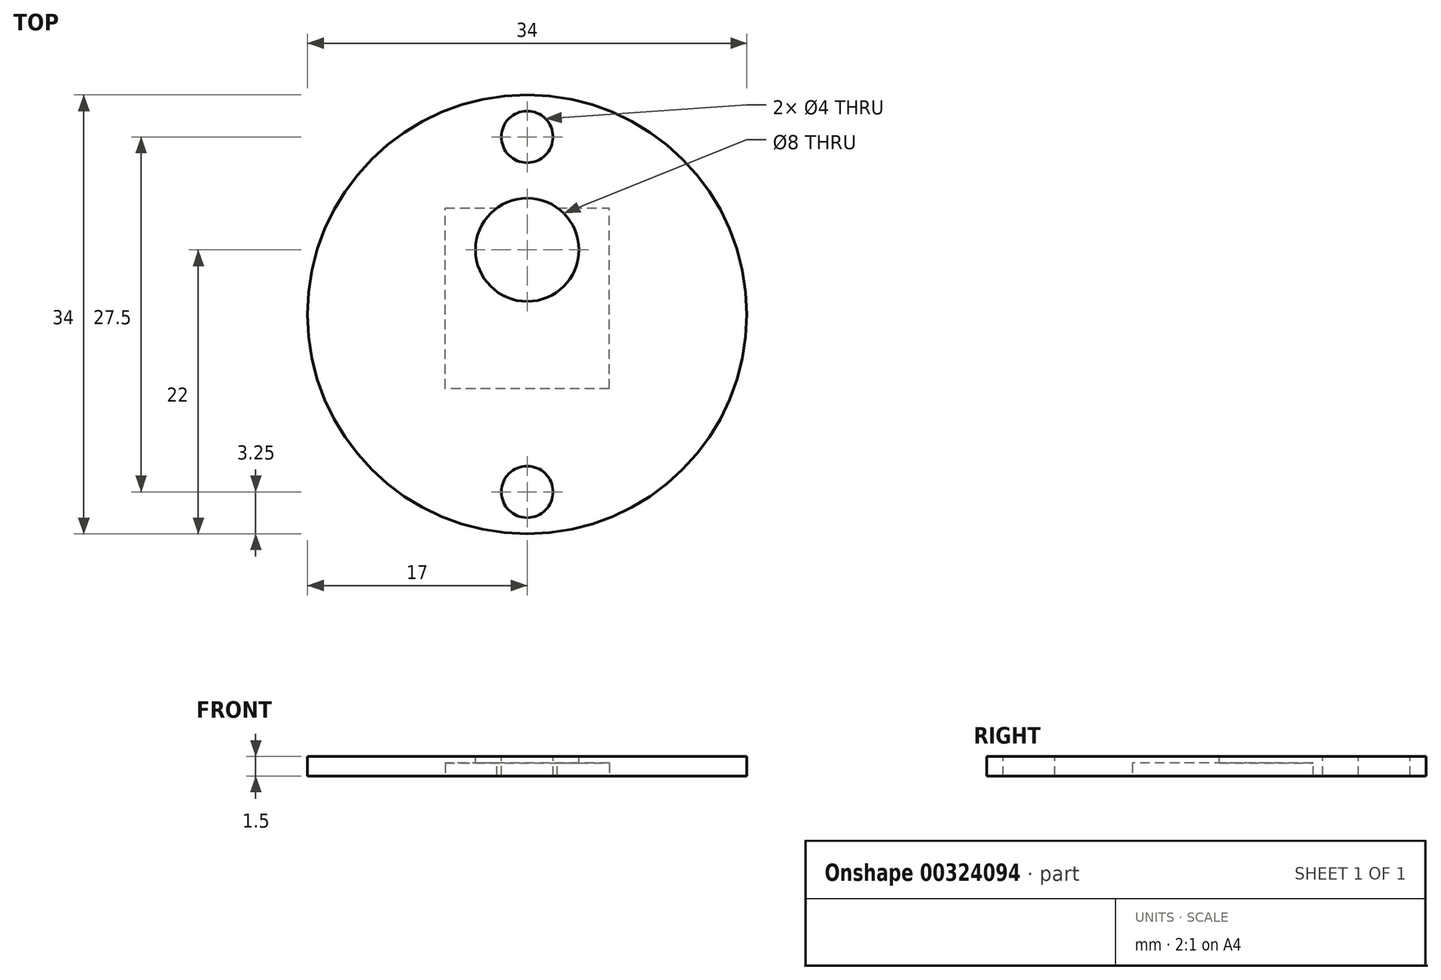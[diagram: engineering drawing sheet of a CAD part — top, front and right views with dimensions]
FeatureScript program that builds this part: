
annotation { "Feature Type Name" : "Feature", "Feature Type Description" : "" }
export const myFeature = defineFeature(function(context is Context, id is Id, definition is map)
    precondition{}
    {
        {
            var Q0;
            Q0=qCreatedBy(makeId("Top.planeOp"),FACE);
            var sketch = newSketch(context, id + "F0", { "sketchPlane" : qUnion([Q0])});
            skCircle(sketch, "E0", {"center": v(0, 0) * mm, "radius": 9.1 * mm});
            skLineSegment(sketch, "E1.bottom", {"start": v(-6.35, 5.75) * mm, "end": v(6.35, 5.75) * mm});
            skLineSegment(sketch, "E1.top", {"start": v(-6.35, -5.75) * mm, "end": v(6.35, -5.75) * mm});
            skLineSegment(sketch, "E1.left", {"start": v(-6.35, 5.75) * mm, "end": v(-6.35, -5.75) * mm});
            skLineSegment(sketch, "E1.right", {"start": v(6.35, 5.75) * mm, "end": v(6.35, -5.75) * mm});
            skSolve(sketch);
        }
        {
            var Q0;
            Q0=makeQuery(id+"F0.imprint","IMPRINT",FACE,{"disambiguationData":[TD([[makeQuery(id+"F0.imprint","IMPRINT",EDGE,{"derivedFrom":sQuery(id+"F0.wireOp",EDGE,"E0")}),1.0]])]});
            extrude(context, id + "F1", {"entities" : qUnion([Q0]), "depth" : 14 * mm});
        }
        {
            var Q0;
            Q0=makeQuery(id+"F1.opExtrude","CAP_FACE",FACE,{"disambiguationData":[OSD([sQuery(id+"F0.wireOp",EDGE,"E0"),sQuery(id+"F0.wireOp",EDGE,"E1.bottom"),sQuery(id+"F0.wireOp",EDGE,"E1.top"),sQuery(id+"F0.wireOp",EDGE,"E1.left"),sQuery(id+"F0.wireOp",EDGE,"E1.right")])],"isStart":true});
            var sketch = newSketch(context, id + "F2", { "sketchPlane" : qUnion([Q0])});
            skLineSegment(sketch, "E2.bottom", {"start": v(6.35, -3.25) * mm, "end": v(-6.35, -3.25) * mm});
            skLineSegment(sketch, "E2.top", {"start": v(6.35, -8.25) * mm, "end": v(-6.35, -8.25) * mm});
            skLineSegment(sketch, "E2.left", {"start": v(6.35, -3.25) * mm, "end": v(6.35, -8.25) * mm});
            skLineSegment(sketch, "E2.right", {"start": v(-6.35, -3.25) * mm, "end": v(-6.35, -8.25) * mm});
            skPoint(sketch, "E2.middle", {"position": v(0, -5.75) * mm});
            skSolve(sketch);
        }
        {
            var Q0;
            {var subQ1=makeQuery(id+"F1.opExtrude","CAP_EDGE",EDGE,{"disambiguationData":[OSD([sQuery(id+"F0.wireOp",EDGE,"E1.bottom")])],"isStart":true});Q0=makeQuery(id+"F2.imprint","IMPRINT",FACE,{"disambiguationData":[TD([[makeQuery(id+"F2.imprint","IMPRINT",EDGE,{"derivedFrom":subQ1}),-1.0]])]});}
            extrude(context, id + "F3", {"entities" : qUnion([Q0]), "operationType" : NewBodyOperationType.REMOVE, "oppositeDirection" : true, "depth" : 5 * mm});
        }
        {
            var Q0;
            Q0=makeQuery(id+"F1.opExtrude","CAP_FACE",FACE,{"disambiguationData":[OSD([sQuery(id+"F0.wireOp",EDGE,"E0"),sQuery(id+"F0.wireOp",EDGE,"E1.bottom"),sQuery(id+"F0.wireOp",EDGE,"E1.top"),sQuery(id+"F0.wireOp",EDGE,"E1.left"),sQuery(id+"F0.wireOp",EDGE,"E1.right")])],"isStart":false});
            cPlane(context, id + "F4", {"entities" : qUnion([Q0]), "cplaneType" : CPlaneType.OFFSET, "offset" : 10 * mm, "oppositeDirection" : true, "width" : 150 * mm, "height" : 150 * mm});
        }
        {
            var Q0;
            Q0=qCreatedBy(id+"F4.planeOp",FACE);
            var sketch = newSketch(context, id + "F5", { "sketchPlane" : qUnion([Q0])});
            skCircle(sketch, "E3", {"center": v(0, 0) * mm, "radius": 17 * mm});
            skCircle(sketch, "E4", {"center": v(0, 0) * mm, "radius": 13.75 * mm, "construction": true});
            skCircle(sketch, "E5", {"center": v(0, 5) * mm, "radius": 4 * mm});
            skCircle(sketch, "E6", {"center": v(0, 13.75) * mm, "radius": 2 * mm});
            skCircle(sketch, "E7", {"center": v(0, -13.75) * mm, "radius": 2 * mm});
            skSolve(sketch);
        }
        {
            var Q0;
            Q0=qSketchRegion(id+"F5",true);
            extrude(context, id + "F6", {"entities" : qUnion([Q0]), "oppositeDirection" : true, "depth" : 1.5 * mm});
        }
        {
            var Q0;
            Q0=makeQuery(id+"F1.opExtrude","SWEPT_BODY",BODY,{"disambiguationData":[OSD([sQuery(id+"F0.wireOp",EDGE,"E0"),sQuery(id+"F0.wireOp",EDGE,"E1.bottom"),sQuery(id+"F0.wireOp",EDGE,"E1.top"),sQuery(id+"F0.wireOp",EDGE,"E1.left"),sQuery(id+"F0.wireOp",EDGE,"E1.right")])]});
            deleteBodies(context, id + "F7", {"entities" : qUnion([Q0])});
        }
        {
            var Q0;
            {var subQ0=sQuery(id+"F2.wireOp",EDGE,"E2.bottom");Q0=makeQuery(id+"F2.imprint","IMPRINT",FACE,{"disambiguationData":[TD([[makeQuery(id+"F2.imprint","IMPRINT",EDGE,{"derivedFrom":subQ0}),-1.0]])]});}
            var Q1;
            {var subQ0=sQuery(id+"F2.wireOp",EDGE,"E2.bottom");Q1=makeQuery(id+"F2.imprint","IMPRINT",FACE,{"disambiguationData":[TD([[makeQuery(id+"F2.imprint","IMPRINT",EDGE,{"derivedFrom":subQ0}),1.0]])]});}
            var Q2;
            {var subQ0=sQuery(id+"F2.wireOp",EDGE,"E2.right");var subQ1=sQuery(id+"F2.wireOp",EDGE,"E2.top");var subQ2=makeQuery(id+"F2.imprint","INTERSECT",VERTEX,{"derivedFrom":[subQ1,subQ0]});Q2=makeQuery(id+"F2.imprint","IMPRINT",FACE,{"disambiguationData":[TD([[makeQuery(id+"F2.imprint","IMPRINT",EDGE,{"disambiguationData":[TD([[subQ2,1.0]])],"derivedFrom":subQ1}),-1.0]])]});}
            var Q3;
            {var subQ1=makeQuery(id+"F1.opExtrude","CAP_EDGE",EDGE,{"disambiguationData":[OSD([sQuery(id+"F0.wireOp",EDGE,"E1.bottom")])],"isStart":true});Q3=makeQuery(id+"F2.imprint","IMPRINT",FACE,{"disambiguationData":[TD([[makeQuery(id+"F2.imprint","IMPRINT",EDGE,{"derivedFrom":subQ1}),-1.0]])]});}
            var Q4;
            {var subQ0=sQuery(id+"F2.wireOp",EDGE,"E2.left");var subQ1=sQuery(id+"F2.wireOp",EDGE,"E2.top");var subQ2=makeQuery(id+"F2.imprint","INTERSECT",VERTEX,{"derivedFrom":[subQ1,subQ0]});Q4=makeQuery(id+"F2.imprint","IMPRINT",FACE,{"disambiguationData":[TD([[makeQuery(id+"F2.imprint","IMPRINT",EDGE,{"disambiguationData":[TD([[subQ2,-1.0]])],"derivedFrom":subQ1}),-1.0]])]});}
            extrude(context, id + "F8", {"entities" : qUnion([Q0, Q1, Q2, Q3, Q4]), "operationType" : NewBodyOperationType.REMOVE, "oppositeDirection" : true, "depth" : 3.5 * mm, "offsetDistance" : 25 * mm});
        }
    });
